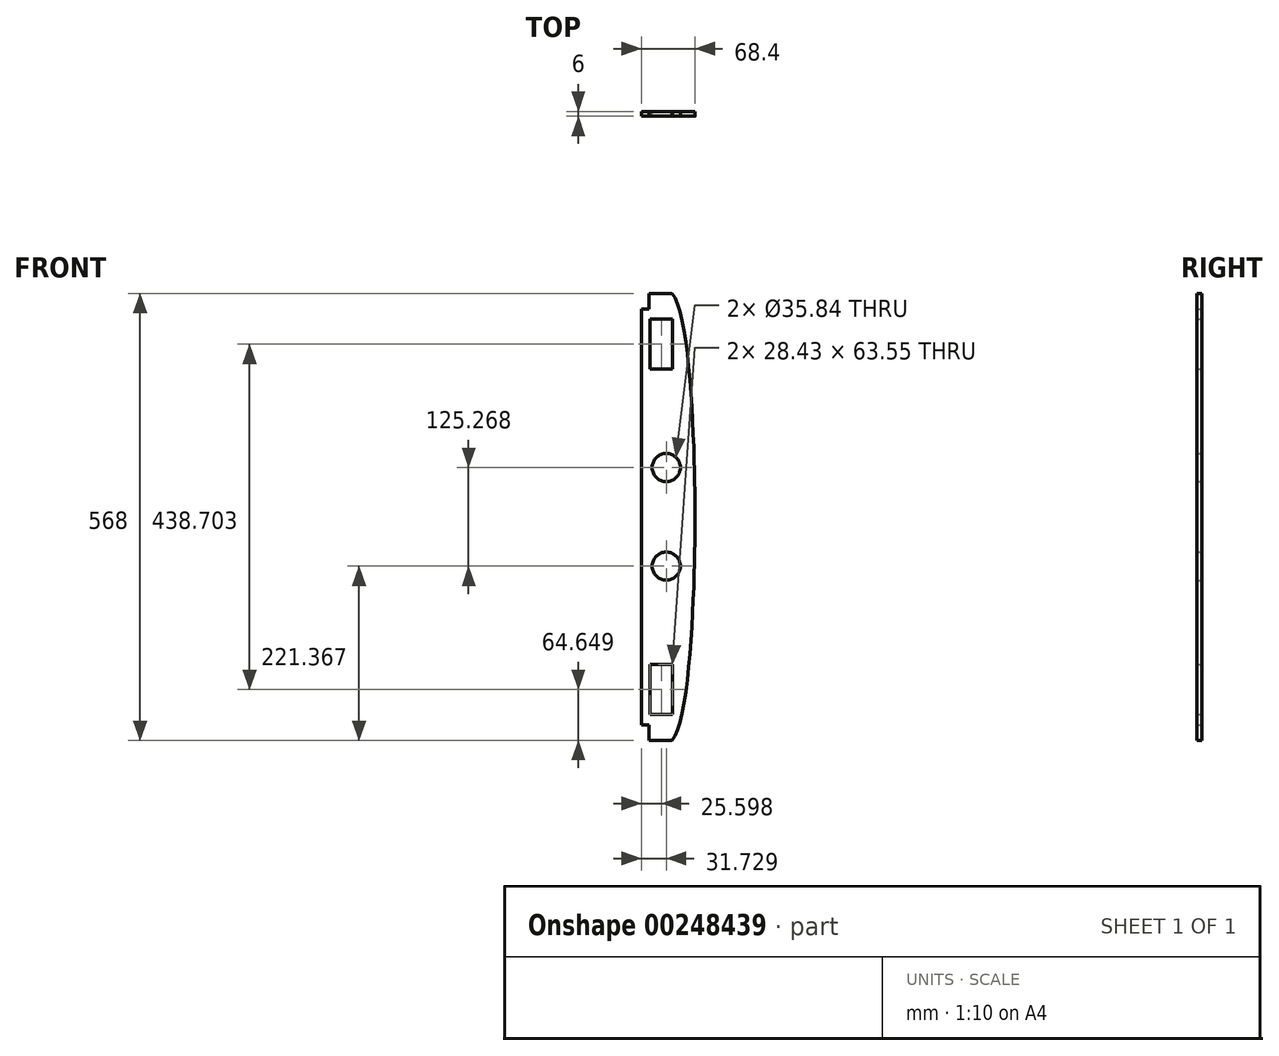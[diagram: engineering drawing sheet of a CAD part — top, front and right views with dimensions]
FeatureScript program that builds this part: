
annotation { "Feature Type Name" : "Feature", "Feature Type Description" : "" }
export const myFeature = defineFeature(function(context is Context, id is Id, definition is map)
    precondition{}
    {
        {
            var Q0;
            Q0=qCreatedBy(makeId("Front.planeOp"),FACE);
            var sketch = newSketch(context, id + "F0", { "sketchPlane" : qUnion([Q0])});
            skLineSegment(sketch, "E0.bottom", {"start": v(183.28, -419.47) * mm, "end": v(124.88, -419.47) * mm});
            skLineSegment(sketch, "E0.top", {"start": v(183.28, 148.53) * mm, "end": v(124.88, 148.53) * mm});
            skLineSegment(sketch, "E0.left", {"start": v(183.28, -419.47) * mm, "end": v(183.28, 148.53) * mm});
            skLineSegment(sketch, "E1", {"start": v(183.28, -419.47) * mm, "end": v(183.28, -135.47) * mm});
            skLineSegment(sketch, "E2", {"start": v(114.88, -135.47) * mm, "end": v(158.04, -135.47) * mm});
            skLineSegment(sketch, "E3", {"start": v(158.04, -135.47) * mm, "end": v(158.04, -140.47) * mm});
            skLineSegment(sketch, "E4", {"start": v(158.04, -135.47) * mm, "end": v(158.04, -130.47) * mm});
            skLineSegment(sketch, "E5", {"start": v(158.04, -135.47) * mm, "end": v(183.28, -135.47) * mm});
            skFitSpline(sketch, "E6", {"points": [v(153.88, 148.53) * mm, v(183.28, -135.47) * mm], "startDerivative": vector(88.2, -102) * mm, "endDerivative": vector(0, -13.58) * mm});
            skFitSpline(sketch, "E7.MirrorCS", {"points": [v(153.88, -419.47) * mm, v(183.28, -135.47) * mm], "startDerivative": vector(88.2, 102) * mm, "endDerivative": vector(0, 13.58) * mm});
            skPoint(sketch, "E8.visualSharp", {"position": v(153.88, 127.63) * mm});
            skPoint(sketch, "E9.MirrorP", {"position": v(153.88, -398.57) * mm});
            skCircle(sketch, "E10", {"center": v(146.6, -72.84) * mm, "radius": 17.92 * mm});
            skCircle(sketch, "E11.MirrorC", {"center": v(146.6, -198.1) * mm, "radius": 17.92 * mm});
            skLineSegment(sketch, "E12", {"start": v(114.88, -135.47) * mm, "end": v(183.28, -135.47) * mm});
            skLineSegment(sketch, "E13", {"start": v(149.08, -135.47) * mm, "end": v(149.08, -140.47) * mm});
            skLineSegment(sketch, "E14", {"start": v(149.08, -135.47) * mm, "end": v(149.08, -130.47) * mm});
            skLineSegment(sketch, "E15", {"start": v(149.08, -130.47) * mm, "end": v(114.88, -130.47) * mm});
            skLineSegment(sketch, "E16", {"start": v(149.08, -140.47) * mm, "end": v(114.88, -140.47) * mm});
            skLineSegment(sketch, "E17", {"start": v(124.88, 148.53) * mm, "end": v(124.88, 128.53) * mm});
            skLineSegment(sketch, "E18", {"start": v(124.88, 128.53) * mm, "end": v(114.88, 128.53) * mm});
            skLineSegment(sketch, "E19", {"start": v(124.88, 148.53) * mm, "end": v(153.88, 148.53) * mm});
            skLineSegment(sketch, "E20.MirrorCS", {"start": v(124.88, -419.47) * mm, "end": v(124.88, -399.47) * mm});
            skLineSegment(sketch, "E21.MirrorCS", {"start": v(124.88, -399.47) * mm, "end": v(114.88, -399.47) * mm});
            skLineSegment(sketch, "E22", {"start": v(114.88, -399.47) * mm, "end": v(114.88, 128.53) * mm});
            skLineSegment(sketch, "E23.bottom", {"start": v(154.7, 115.66) * mm, "end": v(126.26, 115.66) * mm});
            skLineSegment(sketch, "E23.top", {"start": v(154.7, 52.1) * mm, "end": v(126.26, 52.1) * mm});
            skLineSegment(sketch, "E23.left", {"start": v(154.7, 115.66) * mm, "end": v(154.7, 52.1) * mm});
            skLineSegment(sketch, "E23.right", {"start": v(126.26, 115.66) * mm, "end": v(126.26, 52.1) * mm});
            skLineSegment(sketch, "E24.MirrorCS", {"start": v(154.7, -386.6) * mm, "end": v(126.26, -386.6) * mm});
            skLineSegment(sketch, "E25.MirrorCS", {"start": v(154.7, -386.6) * mm, "end": v(154.7, -323.05) * mm});
            skLineSegment(sketch, "E26.MirrorCS", {"start": v(126.26, -386.6) * mm, "end": v(126.26, -323.05) * mm});
            skLineSegment(sketch, "E27.MirrorCS", {"start": v(154.7, -323.05) * mm, "end": v(126.26, -323.05) * mm});
            skSolve(sketch);
        }
        {
            var Q0;
            {var subQ1=sQuery(id+"F0.wireOp",EDGE,"zu24MuOh-8pbl-PKY7-esQD-OuaWEFwxW4IU.bottom");Q0=makeQuery(id+"F0.imprint","IMPRINT",FACE,{"disambiguationData":[TD([[makeQuery(id+"F0.imprint","IMPRINT",EDGE,{"derivedFrom":subQ1}),-1.0]])]});}
            var Q1;
            Q1=makeQuery(id+"F0.imprint","IMPRINT",FACE,{"disambiguationData":[TD([[makeQuery(id+"F0.imprint","IMPRINT",EDGE,{"derivedFrom":sQuery(id+"F0.wireOp",EDGE,"E4")}),-1.0]])]});
            var Q2;
            Q2=makeQuery(id+"F0.imprint","IMPRINT",FACE,{"disambiguationData":[TD([[makeQuery(id+"F0.imprint","IMPRINT",EDGE,{"derivedFrom":sQuery(id+"F0.wireOp",EDGE,"E3")}),1.0]])]});
            var Q3;
            {var subQ2=sQuery(id+"F0.wireOp",EDGE,"E2");Q3=makeQuery(id+"F0.imprint","IMPRINT",FACE,{"disambiguationData":[TD([[makeQuery(id+"F0.imprint","IMPRINT",EDGE,{"derivedFrom":subQ2}),1.0]])]});}
            var Q4;
            {var subQ4=sQuery(id+"F0.wireOp",EDGE,"E2");Q4=makeQuery(id+"F0.imprint","IMPRINT",FACE,{"disambiguationData":[TD([[makeQuery(id+"F0.imprint","IMPRINT",EDGE,{"derivedFrom":subQ4}),-1.0]])]});}
            var Q5;
            {var subQ3=sQuery(id+"F0.wireOp",EDGE,"e991ef47-04eb-4729-9160-831e8e6eb045");Q5=makeQuery(id+"F0.imprint","IMPRINT",FACE,{"disambiguationData":[TD([[makeQuery(id+"F0.imprint","IMPRINT",EDGE,{"derivedFrom":subQ3}),-1.0]])]});}
            var Q6;
            {var subQ3=sQuery(id+"F0.wireOp",EDGE,"E7.MirrorCS");Q6=makeQuery(id+"F0.imprint","IMPRINT",FACE,{"disambiguationData":[TD([[makeQuery(id+"F0.imprint","IMPRINT",EDGE,{"derivedFrom":subQ3}),1.0]])]});}
            var Q7;
            {var subQ6=sQuery(id+"F0.wireOp",EDGE,"E6");Q7=makeQuery(id+"F0.imprint","IMPRINT",FACE,{"disambiguationData":[TD([[makeQuery(id+"F0.imprint","IMPRINT",EDGE,{"derivedFrom":subQ6}),-1.0]])]});}
            extrude(context, id + "F1", {"entities" : qUnion([Q0, Q1, Q2, Q3, Q4, Q5, Q6, Q7]), "depth" : 6 * mm});
        }
    });
